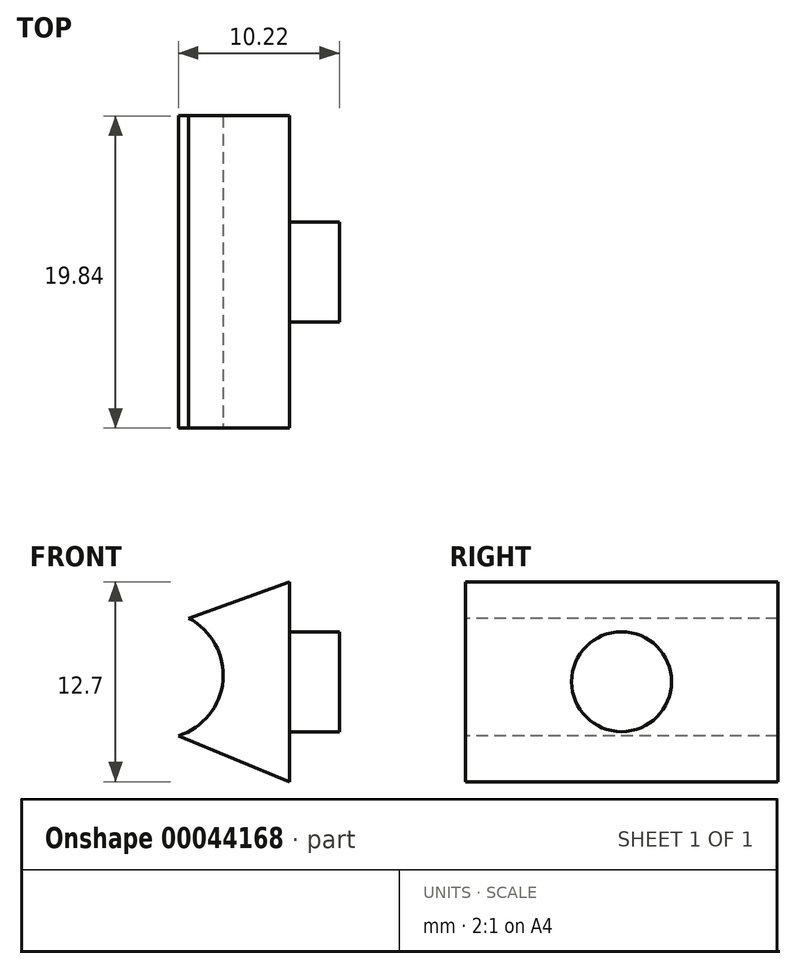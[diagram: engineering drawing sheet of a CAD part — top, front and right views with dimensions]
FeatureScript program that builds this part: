
annotation { "Feature Type Name" : "Feature", "Feature Type Description" : "" }
export const myFeature = defineFeature(function(context is Context, id is Id, definition is map)
    precondition{}
    {
        {
            var Q0;
            Q0=qCreatedBy(makeId("Front.planeOp"),FACE);
            var sketch = newSketch(context, id + "F0", { "sketchPlane" : qUnion([Q0])});
            skLineSegment(sketch, "E0", {"start": v(0, 0) * mm, "end": v(0, 12.7) * mm});
            skArc(sketch, "E1", {"start": v(-7.04, 2.92) * mm, "mid": v(-4.22, 6.43) * mm, "end": v(-6.39, 10.38) * mm});
            skLineSegment(sketch, "E2", {"start": v(0, 0) * mm, "end": v(-7.04, 2.92) * mm});
            skLineSegment(sketch, "E3", {"start": v(0, 12.7) * mm, "end": v(-6.39, 10.38) * mm});
            skSolve(sketch);
        }
        {
            var Q0;
            Q0 = qSketchRegion(id + "F0", true);
            extrude(context, id + "F1", {"entities" : qUnion([Q0]), "oppositeDirection" : true, "depth" : 19.84 * mm});
        }
        {
            var Q0;
            Q0=makeQuery(id+"F1.opExtrude","SWEPT_FACE",FACE,{"disambiguationData":[OSD([sQuery(id+"F0.wireOp",EDGE,"E0")])]});
            var sketch = newSketch(context, id + "F2", { "sketchPlane" : qUnion([Q0])});
            skCircle(sketch, "E4", {"center": v(9.92, 6.35) * mm, "radius": 3.18 * mm});
            skPoint(sketch, "E4.centerSnap0", {"position": v(9.92, 0) * mm});
            skPoint(sketch, "E4.centerSnap1", {"position": v(0, 6.35) * mm});
            skSolve(sketch);
        }
        {
            var Q0;
            Q0 = qSketchRegion(id + "F2", true);
            extrude(context, id + "F3", {"entities" : qUnion([Q0]), "operationType" : NewBodyOperationType.ADD, "depth" : 3.17 * mm});
        }
    });
